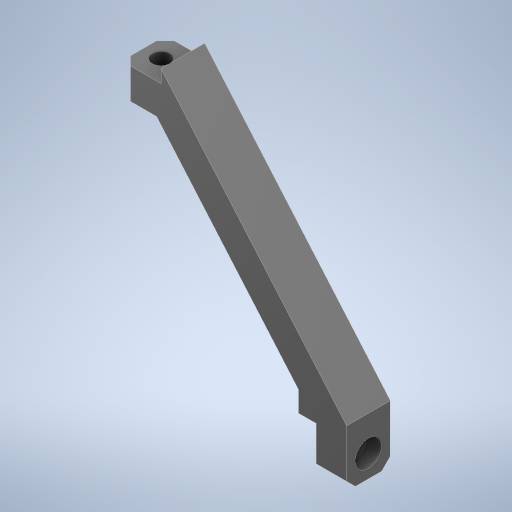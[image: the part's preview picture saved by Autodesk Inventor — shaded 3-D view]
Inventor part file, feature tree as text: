
AUTODESK INVENTOR PART (.ipt)
format: ipt  version: 2024.2 (Build 282272000, 272)  size: 260,096 bytes
history: native  units: in
note: dims shown in document units (in); Inventor stores cm internally (conversion verified against a paired STEP export)
features: extrude x2, sketch x2, chamfer x1, other x1
ambient origin geometry x8: Origin, YZ Plane, XZ Plane, XY Plane, X Axis, Y Axis, Z Axis, Center Point
bodies: Solid1 (feature_tree)
feature tree (6):
  extrude  "Extrusion1"  Depth=0.3937in TaperAngle=0.0deg
  chamfer  "Chamfer1"  Distance=0.0787in Angle=45.0deg
  extrude  "Extrusion2"  Depth=0.1378in
  sketch  "Sketch1"  dims[d0=0.1575in d1=0.3937in d2=0.0in d3=0.0787in d4=0.0787in d5=45.0deg]
  sketch  "Sketch2"  dims[d6=0.1181in d8=0.8973in d9=0.2362in d10=0.1378in d11=0.0in]
  other  "Cortar-Extruir3"
